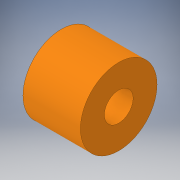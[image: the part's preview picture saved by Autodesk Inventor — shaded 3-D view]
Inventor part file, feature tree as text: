
AUTODESK INVENTOR PART (.ipt)
format: ipt  version: 2017 SP1 (Build 210196100, 196)  size: 96,256 bytes
history: native  units: in
note: dims shown in document units (in); Inventor stores cm internally (conversion verified against a paired STEP export)
features: extrude x1, sketch x1
ambient origin geometry x8: Origin, YZ Plane, XZ Plane, XY Plane, X Axis, Y Axis, Z Axis, Center Point
bodies: Solid1 (feature_tree)
feature tree (2):
  extrude  "Extrusion1"  Depth=0.75in
  sketch  "Sketch1"  dims[d0=0.375in d1=1.0in d2=0.75in d3=0.0in]
